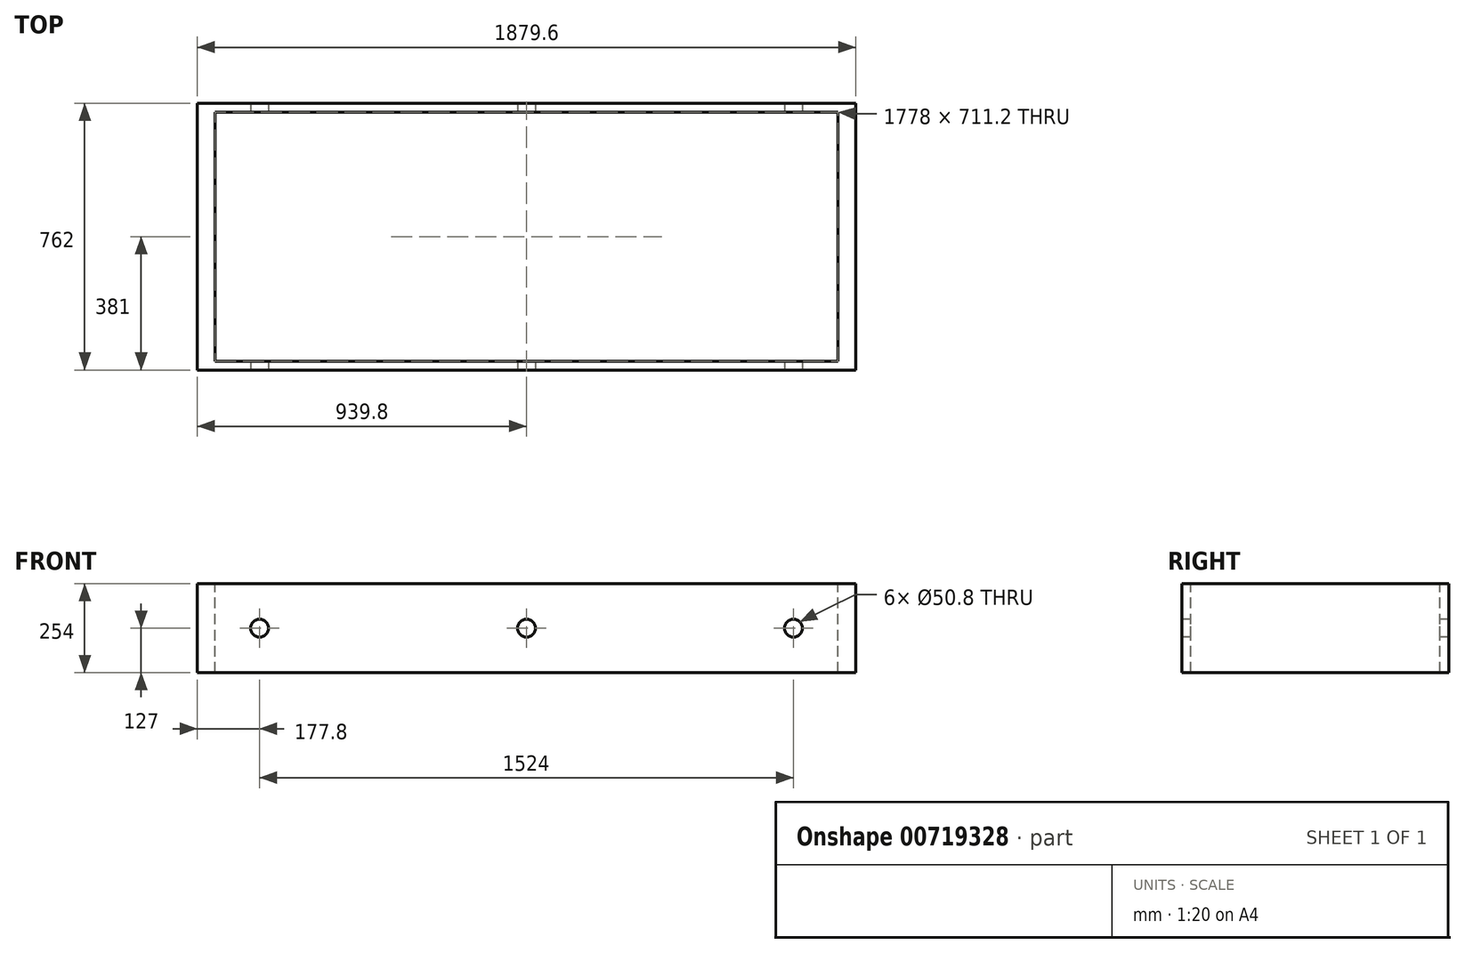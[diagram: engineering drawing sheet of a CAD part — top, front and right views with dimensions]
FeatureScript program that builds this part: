
annotation { "Feature Type Name" : "Feature", "Feature Type Description" : "" }
export const myFeature = defineFeature(function(context is Context, id is Id, definition is map)
    precondition{}
    {
        {
            var Q0;
            Q0=qCreatedBy(makeId("Top.planeOp"),FACE);
            var sketch = newSketch(context, id + "F0", { "sketchPlane" : qUnion([Q0])});
            skLineSegment(sketch, "E0.bottom", {"start": v(-939.8, 381) * mm, "end": v(939.8, 381) * mm});
            skLineSegment(sketch, "E0.top", {"start": v(-939.8, -381) * mm, "end": v(939.8, -381) * mm});
            skLineSegment(sketch, "E0.left", {"start": v(-939.8, 381) * mm, "end": v(-939.8, -381) * mm});
            skLineSegment(sketch, "E0.right", {"start": v(939.8, 381) * mm, "end": v(939.8, -381) * mm});
            skSolve(sketch);
        }
        {
            var Q0;
            Q0 = qSketchRegion(id + "F0", true);
            extrude(context, id + "F1", {"entities" : qUnion([Q0]), "endBound" : BoundingType.SYMMETRIC, "depth" : 254 * mm, "offsetDistance" : 25.4 * mm});
        }
        {
            var Q0;
            Q0=makeQuery(id+"F1.opExtrude","CAP_FACE",FACE,{"disambiguationData":[OSD([sQuery(id+"F0.wireOp",EDGE,"E0.bottom"),sQuery(id+"F0.wireOp",EDGE,"E0.top"),sQuery(id+"F0.wireOp",EDGE,"E0.left"),sQuery(id+"F0.wireOp",EDGE,"E0.right")])],"isStart":false});
            var sketch = newSketch(context, id + "F2", { "sketchPlane" : qUnion([Q0])});
            skLineSegment(sketch, "E1.bottom", {"start": v(-889, 355.6) * mm, "end": v(889, 355.6) * mm});
            skLineSegment(sketch, "E1.top", {"start": v(-889, -355.6) * mm, "end": v(889, -355.6) * mm});
            skLineSegment(sketch, "E1.left", {"start": v(-889, 355.6) * mm, "end": v(-889, -355.6) * mm});
            skLineSegment(sketch, "E1.right", {"start": v(889, 355.6) * mm, "end": v(889, -355.6) * mm});
            skSolve(sketch);
        }
        {
            var Q0;
            Q0 = qSketchRegion(id + "F2", true);
            var Q1;
            Q1 = qSketchRegion(id + "F4", true);
            extrude(context, id + "F3", {"entities" : qUnion([Q0, Q1]), "operationType" : NewBodyOperationType.REMOVE, "endBound" : BoundingType.SYMMETRIC, "oppositeDirection" : true, "depth" : 1270 * mm, "offsetDistance" : 25.4 * mm});
        }
        {
            var Q0;
            Q0=makeQuery(id+"F1.opExtrude","SWEPT_FACE",FACE,{"disambiguationData":[OSD([sQuery(id+"F0.wireOp",EDGE,"E0.top")])]});
            var sketch = newSketch(context, id + "F4", { "sketchPlane" : qUnion([Q0])});
            skCircle(sketch, "E2", {"center": v(-762, 0) * mm, "radius": 25.4 * mm});
            skCircle(sketch, "E3", {"center": v(762, 0) * mm, "radius": 25.4 * mm});
            skCircle(sketch, "E4", {"center": v(0, 0) * mm, "radius": 25.4 * mm});
            skSolve(sketch);
        }
        {
            var Q0;
            Q0 = qSketchRegion(id + "F4", true);
            extrude(context, id + "F5", {"entities" : qUnion([Q0]), "operationType" : NewBodyOperationType.REMOVE, "endBound" : BoundingType.THROUGH_ALL, "oppositeDirection" : true, "depth" : 25.4 * mm, "offsetDistance" : 25.4 * mm});
        }
    });
